# Revit family: NLRS_33_GM_FB_TC_STORAX_vloerluik_BVH-Maxi_BCB
name_source: partatom
category: Generic Models
revit_build: Autodesk Revit 2014 (Build: 20130308_1515(x64)
units: mm (PartAtom-declared; Revit-internal decimal feet)

## types (3) — shared parameters
Manufacturer = Storax
Model = BV
URL = http://www.storax.nl
belasting = 125 kN
binnenluik = tbv betonvulling
brandwerend 90 min = nee
gasdrukveer = nee
geïsoleerd = nee
materiaal = bcb_staal
productgroep = Vloerluiken
rubberen_afdichting = enkel
scharnierend = nee
sluiting = 4
vergrendeling = nee
vullen_met_beton = ja
zero-valued in all types: Default Elevation

## per-type parameters (varying)
| type | binnenmaat_breedte | binnenmaat_lengte | gewicht | uitwendige_breedte | uitwendige_lengte |
| BVH-Maxi 55 | 500 mm  [stored 1.64042 ft] | 500 mm  [stored 1.64042 ft] | 24 | 652 mm | 652 mm |
| BVH-Maxi 66 | 600 mm | 600 mm | 28 | 752 mm | 752 mm |
| BVH-Maxi 88 | 800 mm | 800 mm | 40 | 952 mm  [stored 3.12336 ft] | 952 mm  [stored 3.12336 ft] |

note: [stored X ft] marks values corroborated as IEEE doubles in the binary element streams (Revit-internal decimal feet)

## geometry (parser evidence)
native form markers: Blend x799, Sweep x5
no freeform markers — native parametric forms only
